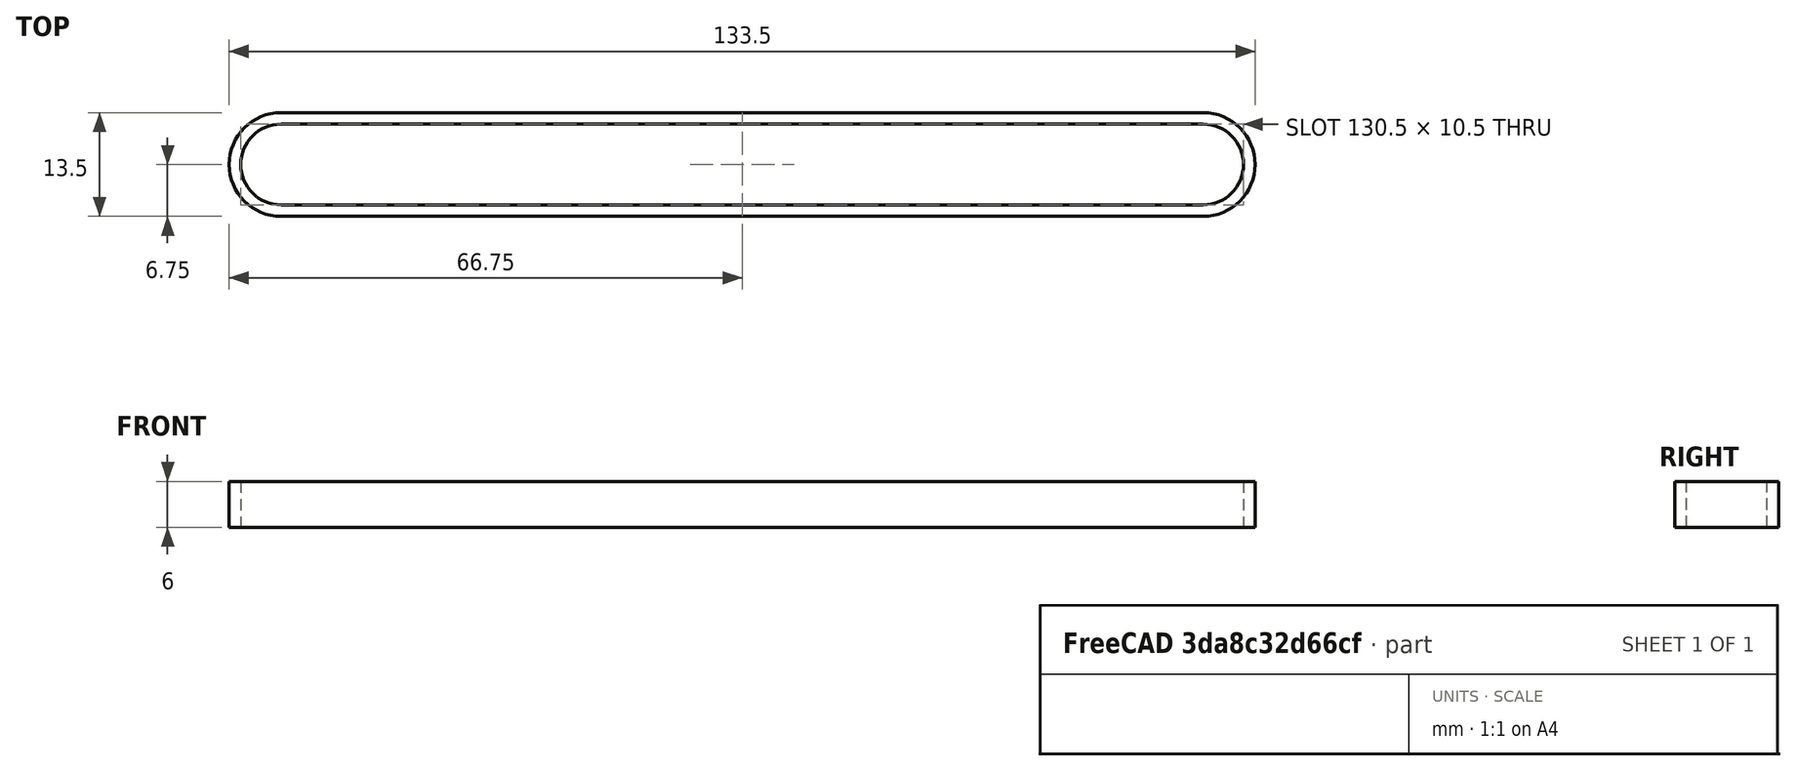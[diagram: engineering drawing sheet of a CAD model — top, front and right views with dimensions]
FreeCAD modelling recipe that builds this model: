
FCSTD DOCUMENT  (FreeCAD 0.14R3310 (Git))
Label: 60. CORREA EJE Z GT2 (SIN DIENTES)
License: CC-BY 3.0
LicenseURL: http://creativecommons.org/licenses/by/3.0/
objects: Sketcher::SketchObject×1, PartDesign::Pad×1
note: 3 computed .brp shape members not serialized (recipe doc carries the construction recipe); baked Part::Feature solids carry a one-line shape summary decoded from their .brp

FEATURE [Sketcher::SketchObject] Sketch
  sketch-geometry (8):
    g0: LineSegment StartX=-60 StartY=6.75 StartZ=0 EndX=60 EndY=6.75 EndZ=0
    g1: ArcOfCircle CenterX=60 CenterY=0 CenterZ=0 NormalX=0 NormalY=0 NormalZ=1 Radius=6.75 StartAngle=4.71239 EndAngle=7.85398
    g2: LineSegment StartX=60 StartY=-6.75 StartZ=0 EndX=-60 EndY=-6.75 EndZ=0
    g3: ArcOfCircle CenterX=-60 CenterY=0 CenterZ=0 NormalX=0 NormalY=0 NormalZ=1 Radius=6.75 StartAngle=1.5708 EndAngle=4.71239
    g4: LineSegment StartX=-60 StartY=-5.25 StartZ=0 EndX=60 EndY=-5.25 EndZ=0
    g5: LineSegment StartX=-60 StartY=5.25 StartZ=0 EndX=60 EndY=5.25 EndZ=0
    g6: ArcOfCircle CenterX=-60 CenterY=0 CenterZ=0 NormalX=0 NormalY=0 NormalZ=1 Radius=5.25 StartAngle=1.5708 EndAngle=4.71239
    g7: ArcOfCircle CenterX=60 CenterY=0 CenterZ=0 NormalX=0 NormalY=0 NormalZ=1 Radius=5.25 StartAngle=4.71239 EndAngle=7.85398
  constraints (25):
    c: Symmetric(g0,g0,g-2)
    c: PointOnObject(g1,g-1)
    c: Coincident(g1,g0)
    c: Tangent(g1,g0)
    c: Radius(g1) = 6.75
    c: Coincident(g2,g1)
    c: Horizontal(g2)
    c: Equal(g2,g0)
    c: Tangent(g2,g1)
    c: PointOnObject(g3,g-1)
    c: Coincident(g3,g0)
    c: Coincident(g3,g2)
    c: Horizontal(g4)
    c: Equal(g4,g0)
    c: Horizontal(g5)
    c: Equal(g5,g4)
    c: Distance(g0) = 120
    c: Coincident(g6,g3)
    c: Coincident(g6,g5)
    c: Coincident(g6,g4)
    c: Coincident(g7,g1)
    c: Coincident(g7,g5)
    c: Coincident(g7,g4)
    c: Tangent(g7,g4)
    c: Radius(g7) = 5.25
FEATURE [PartDesign::Pad] Pad
  Length = 6
  Length2 = 100
  Sketch = -> Sketch
  Type = 0
